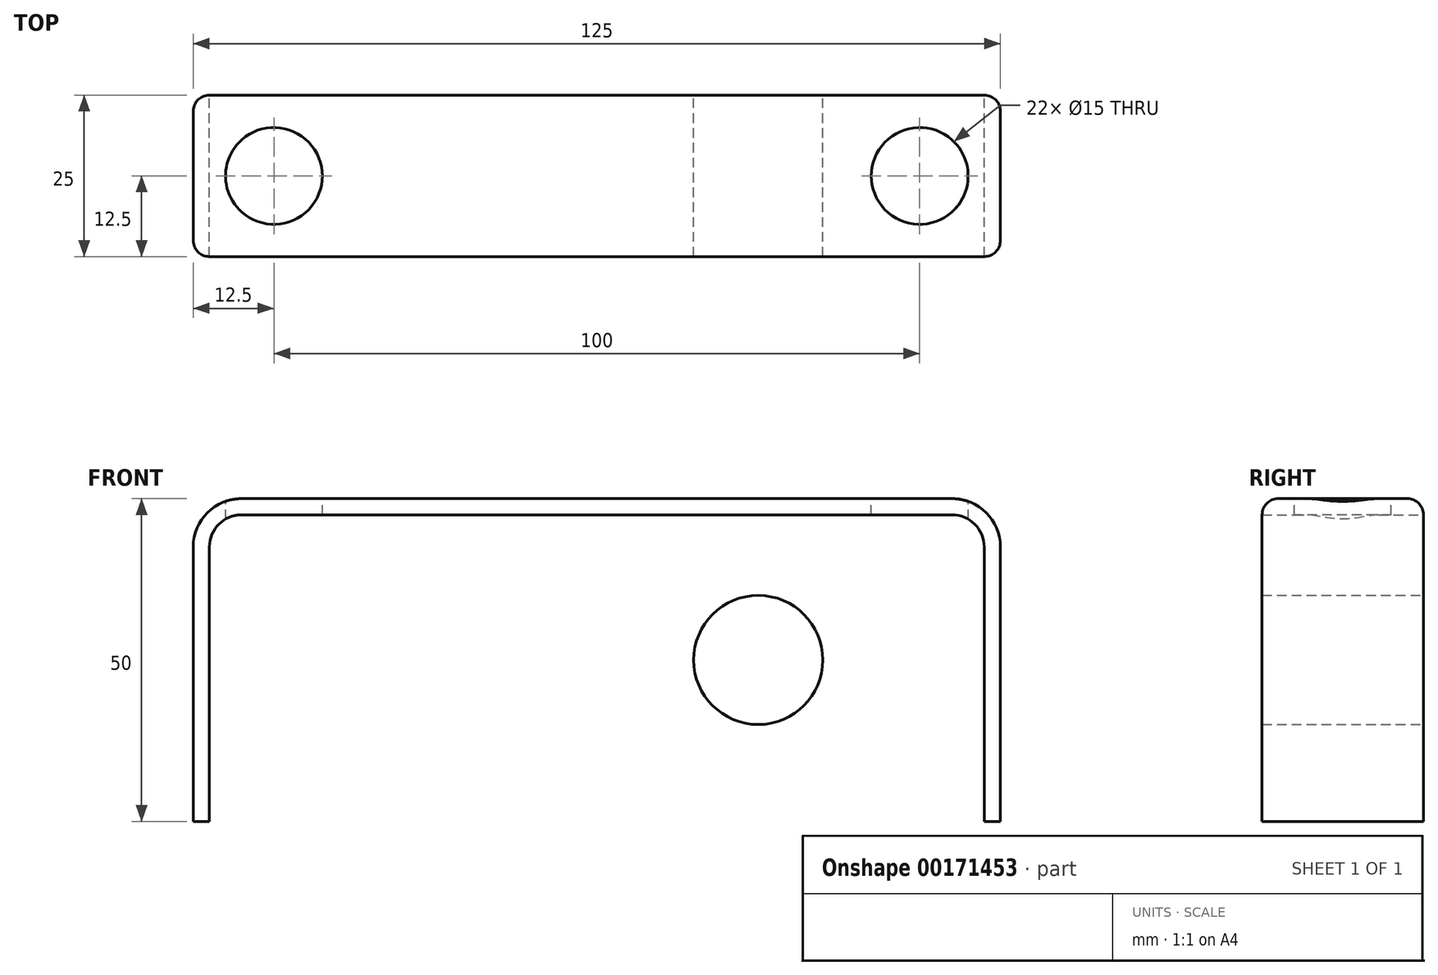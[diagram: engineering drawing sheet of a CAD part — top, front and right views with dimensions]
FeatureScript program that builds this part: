
annotation { "Feature Type Name" : "Feature", "Feature Type Description" : "" }
export const myFeature = defineFeature(function(context is Context, id is Id, definition is map)
    precondition{}
    {
        {
            var Q0;
            Q0=qCreatedBy(makeId("Top.planeOp"),FACE);
            var sketch = newSketch(context, id + "F0", { "sketchPlane" : qUnion([Q0])});
            skLineSegment(sketch, "E0.bottom", {"start": v(0, 0) * mm, "end": v(125, 0) * mm});
            skLineSegment(sketch, "E0.top", {"start": v(0, 25) * mm, "end": v(125, 25) * mm});
            skLineSegment(sketch, "E0.left", {"start": v(0, 0) * mm, "end": v(0, 25) * mm});
            skLineSegment(sketch, "E0.right", {"start": v(125, 0) * mm, "end": v(125, 25) * mm});
            skSolve(sketch);
        }
        {
            var Q0;
            Q0=makeQuery(id+"F0.imprint","IMPRINT",FACE,{"disambiguationData":[TD([[makeQuery(id+"F0.imprint","IMPRINT",EDGE,{"derivedFrom":sQuery(id+"F0.wireOp",EDGE,"E0.bottom")}),1.0]])]});
            extrude(context, id + "F1", {"entities" : qUnion([Q0]), "depth" : 50 * mm});
        }
        {
            var Q0;
            Q0=makeQuery(id+"F1.opExtrude","CAP_EDGE",EDGE,{"disambiguationData":[OSD([sQuery(id+"F0.wireOp",EDGE,"E0.left")])],"isStart":false});
            var Q1;
            Q1=makeQuery(id+"F1.opExtrude","CAP_EDGE",EDGE,{"disambiguationData":[OSD([sQuery(id+"F0.wireOp",EDGE,"E0.right")])],"isStart":false});
            fillet(context, id + "F2", {"entities" : qUnion([Q0, Q1]), "radius" : 7.5 * mm, "tangentPropagation" : true, "allowEdgeOverflow" : false});
        }
        {
            var Q0;
            Q0=makeQuery(id+"F1.opExtrude","SWEPT_EDGE",EDGE,{"disambiguationData":[OSD([sQuery(id+"F0.wireOp",EDGE,"E0.bottom"),sQuery(id+"F0.wireOp",EDGE,"E0.left")])]});
            var Q1;
            Q1=makeQuery(id+"F1.opExtrude","SWEPT_EDGE",EDGE,{"disambiguationData":[OSD([sQuery(id+"F0.wireOp",EDGE,"E0.top"),sQuery(id+"F0.wireOp",EDGE,"E0.left")])]});
            var Q2;
            Q2=makeQuery(id+"F2.opFillet","BLEND_EDGE",EDGE,{"blendedFrom":[makeQuery(id+"F1.opExtrude","CAP_EDGE",EDGE,{"disambiguationData":[OSD([sQuery(id+"F0.wireOp",EDGE,"E0.left")])],"isStart":false}),makeQuery(id+"F1.opExtrude","SWEPT_FACE",FACE,{"disambiguationData":[OSD([sQuery(id+"F0.wireOp",EDGE,"E0.bottom")])]})],"blendedInto":[makeQuery(id+"F1.opExtrude","SWEPT_FACE",FACE,{"disambiguationData":[OSD([sQuery(id+"F0.wireOp",EDGE,"E0.bottom")])]})]});
            var Q3;
            Q3=makeQuery(id+"F1.opExtrude","CAP_EDGE",EDGE,{"disambiguationData":[OSD([sQuery(id+"F0.wireOp",EDGE,"E0.bottom")])],"isStart":false});
            var Q4;
            Q4=makeQuery(id+"F2.opFillet","BLEND_EDGE",EDGE,{"blendedFrom":[makeQuery(id+"F1.opExtrude","CAP_EDGE",EDGE,{"disambiguationData":[OSD([sQuery(id+"F0.wireOp",EDGE,"E0.left")])],"isStart":false}),makeQuery(id+"F1.opExtrude","SWEPT_FACE",FACE,{"disambiguationData":[OSD([sQuery(id+"F0.wireOp",EDGE,"E0.top")])]})],"blendedInto":[makeQuery(id+"F1.opExtrude","SWEPT_FACE",FACE,{"disambiguationData":[OSD([sQuery(id+"F0.wireOp",EDGE,"E0.top")])]})]});
            var Q5;
            Q5=makeQuery(id+"F1.opExtrude","CAP_EDGE",EDGE,{"disambiguationData":[OSD([sQuery(id+"F0.wireOp",EDGE,"E0.top")])],"isStart":false});
            var Q6;
            Q6=makeQuery(id+"F2.opFillet","BLEND_EDGE",EDGE,{"blendedFrom":[makeQuery(id+"F1.opExtrude","CAP_EDGE",EDGE,{"disambiguationData":[OSD([sQuery(id+"F0.wireOp",EDGE,"E0.right")])],"isStart":false}),makeQuery(id+"F1.opExtrude","SWEPT_FACE",FACE,{"disambiguationData":[OSD([sQuery(id+"F0.wireOp",EDGE,"E0.top")])]})],"blendedInto":[makeQuery(id+"F1.opExtrude","SWEPT_FACE",FACE,{"disambiguationData":[OSD([sQuery(id+"F0.wireOp",EDGE,"E0.top")])]})]});
            var Q7;
            Q7=makeQuery(id+"F1.opExtrude","SWEPT_EDGE",EDGE,{"disambiguationData":[OSD([sQuery(id+"F0.wireOp",EDGE,"E0.top"),sQuery(id+"F0.wireOp",EDGE,"E0.right")])]});
            var Q8;
            Q8=makeQuery(id+"F1.opExtrude","SWEPT_EDGE",EDGE,{"disambiguationData":[OSD([sQuery(id+"F0.wireOp",EDGE,"E0.bottom"),sQuery(id+"F0.wireOp",EDGE,"E0.right")])]});
            var Q9;
            Q9=makeQuery(id+"F2.opFillet","BLEND_EDGE",EDGE,{"blendedFrom":[makeQuery(id+"F1.opExtrude","CAP_EDGE",EDGE,{"disambiguationData":[OSD([sQuery(id+"F0.wireOp",EDGE,"E0.right")])],"isStart":false}),makeQuery(id+"F1.opExtrude","SWEPT_FACE",FACE,{"disambiguationData":[OSD([sQuery(id+"F0.wireOp",EDGE,"E0.bottom")])]})],"blendedInto":[makeQuery(id+"F1.opExtrude","SWEPT_FACE",FACE,{"disambiguationData":[OSD([sQuery(id+"F0.wireOp",EDGE,"E0.bottom")])]})]});
            fillet(context, id + "F3", {"entities" : qUnion([Q0, Q1, Q2, Q3, Q4, Q5, Q6, Q7, Q8, Q9]), "radius" : 2.5 * mm, "tangentPropagation" : true, "allowEdgeOverflow" : false});
        }
        {
            var Q0;
            Q0=makeQuery(id+"F1.opExtrude","SWEPT_FACE",FACE,{"disambiguationData":[OSD([sQuery(id+"F0.wireOp",EDGE,"E0.top")])]});
            var sketch = newSketch(context, id + "F4", { "sketchPlane" : qUnion([Q0])});
            skLineSegment(sketch, "E1", {"start": v(-62.5, 0) * mm, "end": v(-62.5, 47.5) * mm, "construction": true});
            skLineSegment(sketch, "E2", {"start": v(-122.5, 25) * mm, "end": v(-2.5, 25) * mm, "construction": true});
            skCircle(sketch, "E3", {"center": v(-37.5, 25) * mm, "radius": 10 * mm});
            skCircle(sketch, "E4.MirrorC", {"center": v(-87.5, 25) * mm, "radius": 10 * mm});
            skSolve(sketch);
        }
        {
            var Q0;
            Q0=makeQuery(id+"F4.imprint","IMPRINT",FACE,{"disambiguationData":[TD([[makeQuery(id+"F4.imprint","IMPRINT",EDGE,{"derivedFrom":sQuery(id+"F4.wireOp",EDGE,"E4.MirrorC")}),-1.0]])]});
            var Q1;
            Q1=makeQuery(id+"F4.imprint","IMPRINT",FACE,{"disambiguationData":[TD([[makeQuery(id+"F4.imprint","IMPRINT",EDGE,{"derivedFrom":sQuery(id+"F4.wireOp",EDGE,"E3")}),1.0]])]});
            var Q2;
            Q2=makeQuery(id+"F1.opExtrude","SWEPT_FACE",FACE,{"disambiguationData":[OSD([sQuery(id+"F0.wireOp",EDGE,"E0.bottom")])]});
            extrude(context, id + "F5", {"entities" : qUnion([Q0, Q1]), "operationType" : NewBodyOperationType.REMOVE, "endBound" : BoundingType.UP_TO_SURFACE, "oppositeDirection" : true, "endBoundEntityFace" : qUnion([Q2]), "depth" : 36.7 * mm});
        }
        {
            var Q0;
            Q0=makeQuery(id+"F1.opExtrude","CAP_FACE",FACE,{"disambiguationData":[OSD([sQuery(id+"F0.wireOp",EDGE,"E0.bottom"),sQuery(id+"F0.wireOp",EDGE,"E0.top"),sQuery(id+"F0.wireOp",EDGE,"E0.left"),sQuery(id+"F0.wireOp",EDGE,"E0.right")])],"isStart":false});
            var sketch = newSketch(context, id + "F6", { "sketchPlane" : qUnion([Q0])});
            skPoint(sketch, "E5", {"position": v(112.5, 12.5) * mm});
            skPoint(sketch, "E5.positionSnap0", {"position": v(117.5, 12.5) * mm});
            skLineSegment(sketch, "E6", {"start": v(62.5, 22.5) * mm, "end": v(62.5, 2.5) * mm, "construction": true});
            skPoint(sketch, "E7.MirrorP", {"position": v(12.5, 12.5) * mm});
            skSolve(sketch);
        }
        {
            var Q0;
            Q0=sQuery(id+"F6.wireOp",VERTEX,"E5");
            var Q1;
            Q1=sQuery(id+"F6.wireOp",VERTEX,"E7.MirrorP");
            var Q2;
            Q2=makeQuery(id+"F1.opExtrude","SWEPT_BODY",BODY,{"disambiguationData":[OSD([sQuery(id+"F0.wireOp",EDGE,"E0.bottom"),sQuery(id+"F0.wireOp",EDGE,"E0.top"),sQuery(id+"F0.wireOp",EDGE,"E0.left"),sQuery(id+"F0.wireOp",EDGE,"E0.right")])]});
            hole(context, id + "F7", {"style" : HoleStyle.C_BORE, "endStyle" : HoleEndStyle.THROUGH, "holeDiameter" : 6 * mm, "cBoreDiameter" : 15 * mm, "cBoreDepth" : 20 * mm, "locations" : qUnion([Q0, Q1]), "scope" : qUnion([Q2]), "isTappedThrough" : true});
        }
    });
